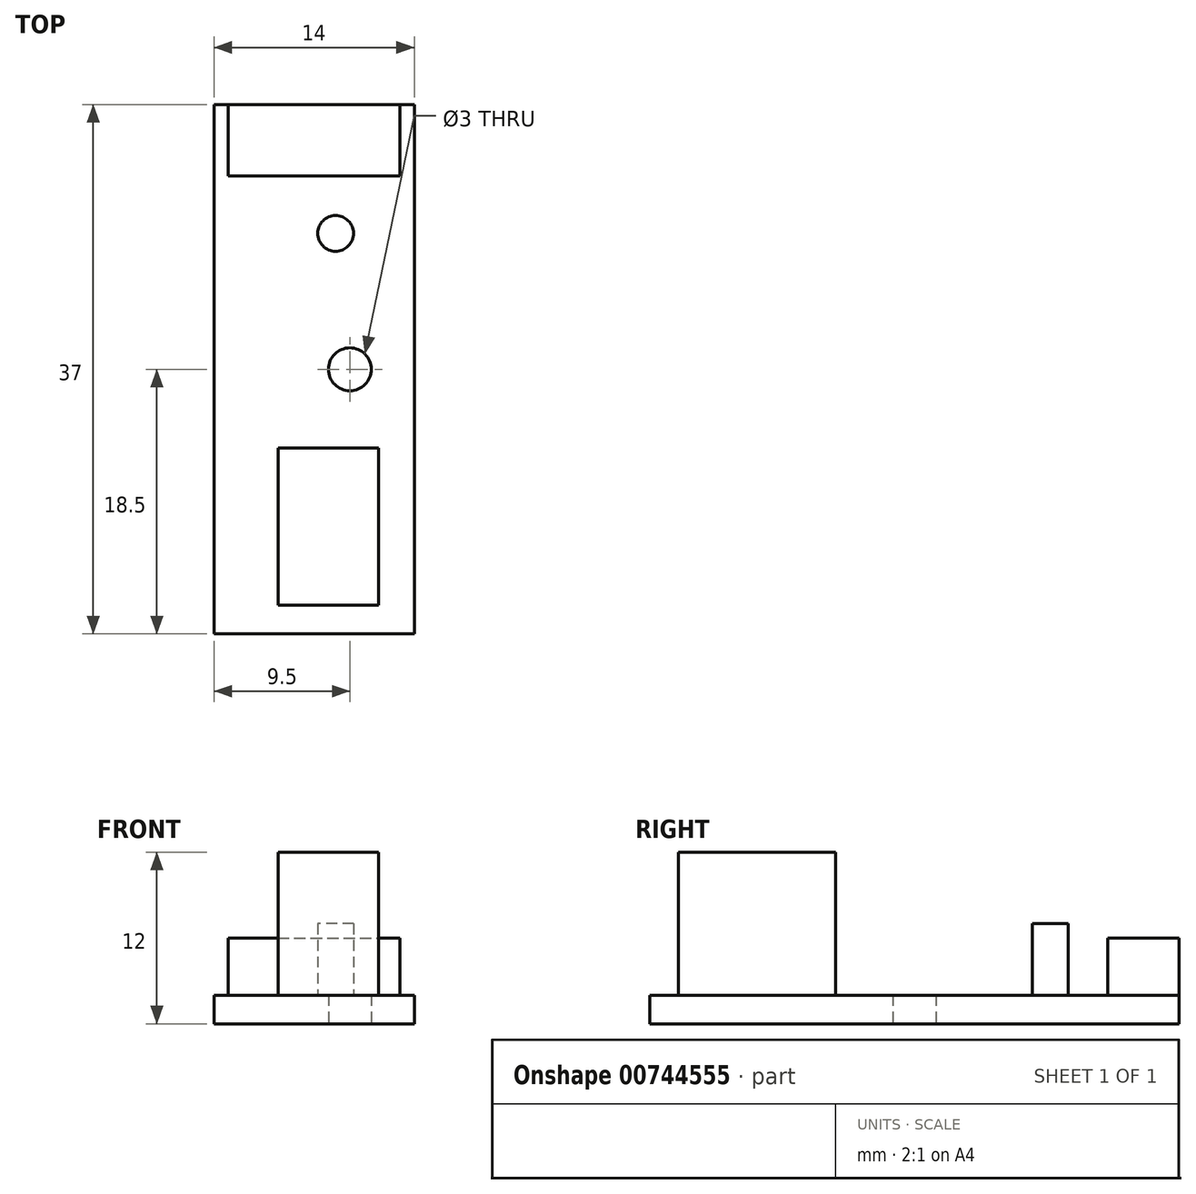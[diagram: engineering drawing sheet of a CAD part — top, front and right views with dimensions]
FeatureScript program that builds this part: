
annotation { "Feature Type Name" : "Feature", "Feature Type Description" : "" }
export const myFeature = defineFeature(function(context is Context, id is Id, definition is map)
    precondition{}
    {
        {
            var Q0;
            Q0=qCreatedBy(makeId("Top.planeOp"),FACE);
            var sketch = newSketch(context, id + "F0", { "sketchPlane" : qUnion([Q0])});
            skLineSegment(sketch, "E0.bottom", {"start": v(-9.5, 18.5) * mm, "end": v(4.5, 18.5) * mm});
            skLineSegment(sketch, "E0.top", {"start": v(-9.5, -18.5) * mm, "end": v(4.5, -18.5) * mm});
            skLineSegment(sketch, "E0.left", {"start": v(-9.5, 18.5) * mm, "end": v(-9.5, -18.5) * mm});
            skLineSegment(sketch, "E0.right", {"start": v(4.5, 18.5) * mm, "end": v(4.5, -18.5) * mm});
            skCircle(sketch, "E1", {"center": v(0, 0) * mm, "radius": 1.5 * mm});
            skSolve(sketch);
        }
        {
            var Q0;
            Q0 = qSketchRegion(id + "F0", true);
            extrude(context, id + "F1", {"entities" : qUnion([Q0]), "depth" : 2 * mm, "offsetDistance" : 25 * mm});
        }
        {
            var Q0;
            Q0=makeQuery(id+"F1.opExtrude","CAP_FACE",FACE,{"disambiguationData":[OSD([sQuery(id+"F0.wireOp",EDGE,"E0.bottom"),sQuery(id+"F0.wireOp",EDGE,"E0.top"),sQuery(id+"F0.wireOp",EDGE,"E0.left"),sQuery(id+"F0.wireOp",EDGE,"E0.right"),sQuery(id+"F0.wireOp",EDGE,"E1")])],"isStart":false});
            var sketch = newSketch(context, id + "F2", { "sketchPlane" : qUnion([Q0])});
            skLineSegment(sketch, "E2.bottom", {"start": v(-8.5, 18.5) * mm, "end": v(3.5, 18.5) * mm});
            skLineSegment(sketch, "E2.top", {"start": v(-8.5, 13.5) * mm, "end": v(3.5, 13.5) * mm});
            skLineSegment(sketch, "E2.left", {"start": v(-8.5, 18.5) * mm, "end": v(-8.5, 13.5) * mm});
            skLineSegment(sketch, "E2.right", {"start": v(3.5, 18.5) * mm, "end": v(3.5, 13.5) * mm});
            skLineSegment(sketch, "E3", {"start": v(-2.5, -18.5) * mm, "end": v(-2.5, 18.5) * mm, "construction": true});
            skSolve(sketch);
        }
        {
            var Q0;
            Q0 = qSketchRegion(id + "F2", true);
            extrude(context, id + "F3", {"entities" : qUnion([Q0]), "operationType" : NewBodyOperationType.ADD, "depth" : 4 * mm, "offsetDistance" : 25 * mm});
        }
        {
            var Q0;
            Q0=makeQuery(id+"F1.opExtrude","CAP_FACE",FACE,{"disambiguationData":[OSD([sQuery(id+"F0.wireOp",EDGE,"E0.bottom"),sQuery(id+"F0.wireOp",EDGE,"E0.top"),sQuery(id+"F0.wireOp",EDGE,"E0.left"),sQuery(id+"F0.wireOp",EDGE,"E0.right"),sQuery(id+"F0.wireOp",EDGE,"E1")])],"isStart":false});
            var sketch = newSketch(context, id + "F4", { "sketchPlane" : qUnion([Q0])});
            skCircle(sketch, "E4", {"center": v(-1, 9.5) * mm, "radius": 1.25 * mm});
            skSolve(sketch);
        }
        {
            var Q0;
            Q0 = qSketchRegion(id + "F4", true);
            extrude(context, id + "F5", {"entities" : qUnion([Q0]), "operationType" : NewBodyOperationType.ADD, "depth" : 5 * mm, "offsetDistance" : 25 * mm});
        }
        {
            var Q0;
            Q0=makeQuery(id+"F1.opExtrude","CAP_FACE",FACE,{"disambiguationData":[OSD([sQuery(id+"F0.wireOp",EDGE,"E0.bottom"),sQuery(id+"F0.wireOp",EDGE,"E0.top"),sQuery(id+"F0.wireOp",EDGE,"E0.left"),sQuery(id+"F0.wireOp",EDGE,"E0.right"),sQuery(id+"F0.wireOp",EDGE,"E1")])],"isStart":false});
            var sketch = newSketch(context, id + "F6", { "sketchPlane" : qUnion([Q0])});
            skLineSegment(sketch, "E5.bottom", {"start": v(-5, -5.5) * mm, "end": v(2, -5.5) * mm});
            skLineSegment(sketch, "E5.top", {"start": v(-5, -16.5) * mm, "end": v(2, -16.5) * mm});
            skLineSegment(sketch, "E5.left", {"start": v(-5, -5.5) * mm, "end": v(-5, -16.5) * mm});
            skLineSegment(sketch, "E5.right", {"start": v(2, -5.5) * mm, "end": v(2, -16.5) * mm});
            skSolve(sketch);
        }
        {
            var Q0;
            Q0 = qSketchRegion(id + "F6", true);
            extrude(context, id + "F7", {"entities" : qUnion([Q0]), "operationType" : NewBodyOperationType.ADD, "depth" : 10 * mm, "offsetDistance" : 25 * mm});
        }
    });
